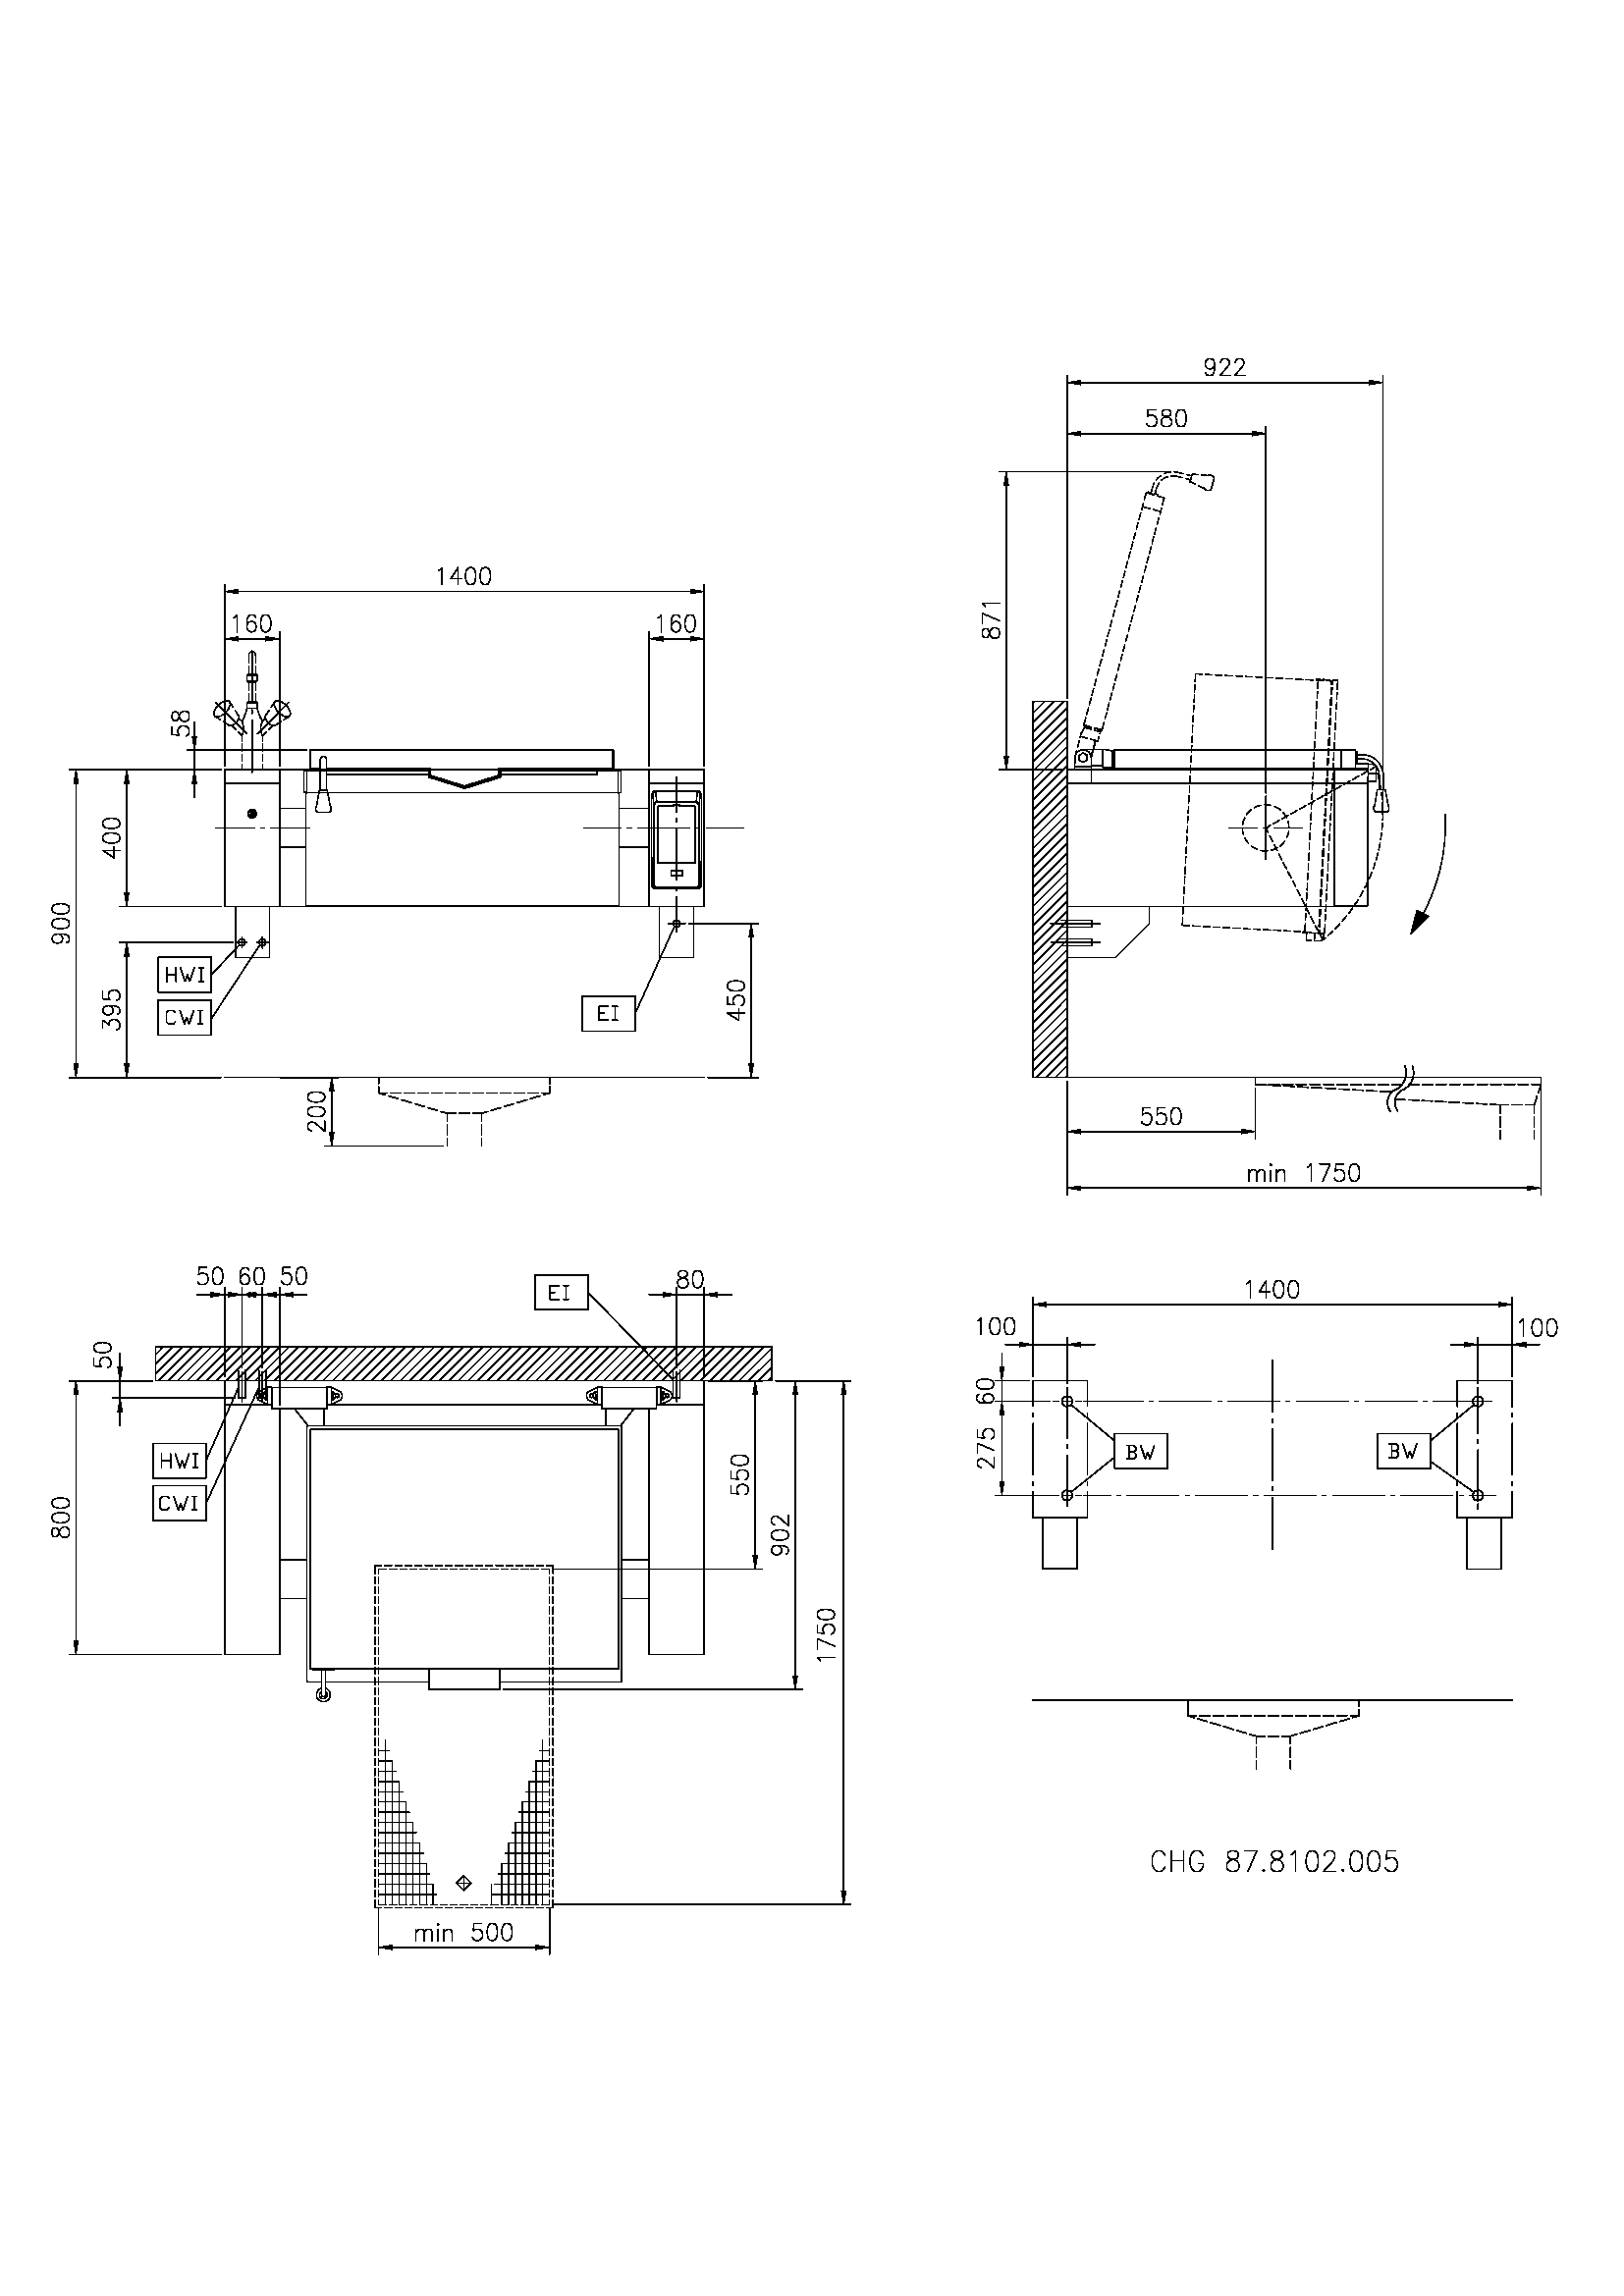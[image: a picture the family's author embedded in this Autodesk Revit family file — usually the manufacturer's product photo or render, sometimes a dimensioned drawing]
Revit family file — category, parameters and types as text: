
# Revit family: QF_ELECTROLUXPROFESSIONAL_586285_PFET08EUEO
name_source: partatom
category: Attrezzature speciali
units: mm (PartAtom-declared; Revit-internal decimal feet)

## family parameters
Basato su piano di lavoro = No
Condiviso = No
Punto di calcolo locali = No
Quota connettore circolare = Usa diametro
Sempre verticale = Sì
Taglio con vuoti quando caricato = No
Tipo di parte = Normale

## types (1)
- Standard
    Accessory = Sì
    Cold Water Size = 13 mm
    Compressed Air Pressure = 0.0 Pa
    Compressed Air Size = 0 mm
    Compressed Air Volume = 0.0 L/s
    Condensate Return Size = 0 mm
    Cycle = 50 Hz
    Depth Actual = 850 mm  [stored 2.78871 ft]
    Descrizione = ELECTRIC TILTING BRAISING PAN, 80L, COMPOUND, WALL,D850
    Direct Waste Size = 0 mm
    Gas Input Pressure = 0
    Gas KW = 0
    Gas Size = 0 mm
    HP = 27.6 HP
    Height Actual = 400 mm  [stored 1.31234 ft]
    Hot Water Size = 13 mm
    Item Number = 586285
    Length Actual = 1400 mm  [stored 4.59318 ft]
    Modello = PFET08EUEO
    Phase = 3
    Produttore = Electrolux Professional
    Prospetto di default = 0 mm  [stored 0 ft]
    Refrigerant Compressor Remote = Sì
    Refrigeration Liquid Line Size = 0 mm  [stored 0 ft]
    Refrigeration Suction Line Size = 0 mm  [stored 0 ft]
    Steam Consumption per Hour = 0
    Steam Supply Maximum Pressure = 0.0 Pa
    Steam Supply Minimum Pressure = 0.0 Pa
    Steam Supply Size = 0 mm
    URL = https://www.electroluxprofessional.com
    URL Manufacturer = https://www.electroluxprofessional.com
    Volts = 400 V
    Watts = 20600 W
    Weight = 240.00 kg

note: source unit labels omitted for Gas Input Pressure — the stored unit's dimension contradicts the parameter name (converter mislabeling)

note: [stored X ft] marks values corroborated as IEEE doubles in the binary element streams (Revit-internal decimal feet)

## geometry (parser evidence)
native form markers: Blend x10, Sweep x9
no freeform markers — native parametric forms only
